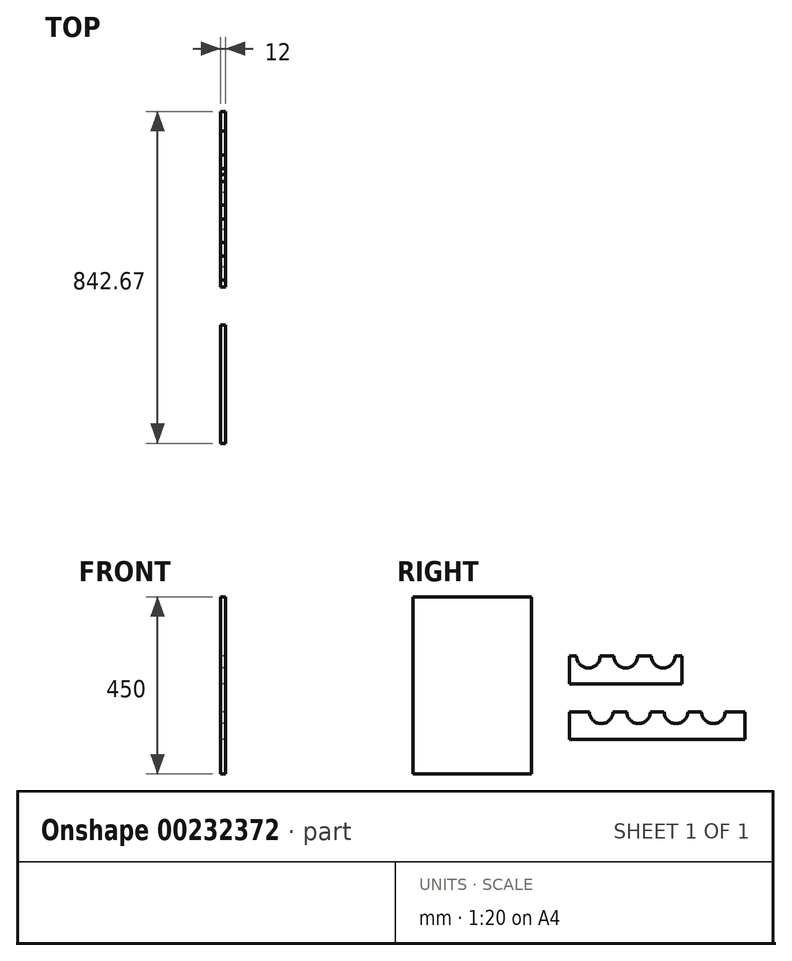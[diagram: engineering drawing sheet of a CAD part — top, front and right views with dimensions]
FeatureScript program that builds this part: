
annotation { "Feature Type Name" : "Feature", "Feature Type Description" : "" }
export const myFeature = defineFeature(function(context is Context, id is Id, definition is map)
    precondition{}
    {
        {
            var Q0;
            Q0=qCreatedBy(makeId("Right.planeOp"),FACE);
            var sketch = newSketch(context, id + "F0", { "sketchPlane" : qUnion([Q0])});
            skLineSegment(sketch, "E0", {"start": v(0, 0) * mm, "end": v(0, 70) * mm});
            skLineSegment(sketch, "E1", {"start": v(0, 70) * mm, "end": v(17.5, 70) * mm});
            skArc(sketch, "E2", {"start": v(17.5, 70) * mm, "mid": v(47.5, 40) * mm, "end": v(77.5, 70) * mm});
            skArc(sketch, "E3.1.0.0", {"start": v(112.5, 70) * mm, "mid": v(142.5, 40) * mm, "end": v(172.5, 70) * mm});
            skArc(sketch, "E3.2.0.0", {"start": v(207.5, 70) * mm, "mid": v(237.5, 40) * mm, "end": v(267.5, 70) * mm});
            skLineSegment(sketch, "E3.direction1", {"start": v(17.5, 70) * mm, "end": v(112.5, 70) * mm, "construction": true});
            skLineSegment(sketch, "E4", {"start": v(77.5, 70) * mm, "end": v(112.5, 70) * mm});
            skLineSegment(sketch, "E5", {"start": v(172.5, 70) * mm, "end": v(207.5, 70) * mm});
            skLineSegment(sketch, "E6", {"start": v(267.5, 70) * mm, "end": v(285, 70) * mm});
            skLineSegment(sketch, "E7", {"start": v(285, 70) * mm, "end": v(285, 0) * mm});
            skLineSegment(sketch, "E8", {"start": v(285, 0) * mm, "end": v(0, 0) * mm});
            skSolve(sketch);
        }
        {
            var Q0;
            Q0 = qSketchRegion(id + "F0", true);
            extrude(context, id + "F1", {"entities" : qUnion([Q0]), "depth" : 12 * mm});
        }
        {
            var Q0;
            Q0=qCreatedBy(makeId("Right.planeOp"),FACE);
            var sketch = newSketch(context, id + "F2", { "sketchPlane" : qUnion([Q0])});
            skLineSegment(sketch, "E9", {"start": v(0, -71.43) * mm, "end": v(0, -141.43) * mm});
            skLineSegment(sketch, "E10", {"start": v(0, -141.43) * mm, "end": v(445, -141.43) * mm});
            skLineSegment(sketch, "E11", {"start": v(445, -141.43) * mm, "end": v(445, -71.43) * mm});
            skLineSegment(sketch, "E12", {"start": v(0, -71.43) * mm, "end": v(50, -71.43) * mm});
            skArc(sketch, "E13", {"start": v(50, -71.43) * mm, "mid": v(80, -101.43) * mm, "end": v(110, -71.43) * mm});
            skArc(sketch, "E14.1.0.0", {"start": v(145, -71.43) * mm, "mid": v(175, -101.43) * mm, "end": v(205, -71.43) * mm});
            skArc(sketch, "E14.2.0.0", {"start": v(240, -71.43) * mm, "mid": v(270, -101.43) * mm, "end": v(300, -71.43) * mm});
            skArc(sketch, "E14.3.0.0", {"start": v(335, -71.43) * mm, "mid": v(365, -101.43) * mm, "end": v(395, -71.43) * mm});
            skLineSegment(sketch, "E14.direction1", {"start": v(50, -71.43) * mm, "end": v(145, -71.43) * mm, "construction": true});
            skLineSegment(sketch, "E15", {"start": v(110, -71.43) * mm, "end": v(145, -71.43) * mm});
            skLineSegment(sketch, "E16", {"start": v(205, -71.43) * mm, "end": v(240, -71.43) * mm});
            skLineSegment(sketch, "E17", {"start": v(300, -71.43) * mm, "end": v(335, -71.43) * mm});
            skLineSegment(sketch, "E18", {"start": v(395, -71.43) * mm, "end": v(445, -71.43) * mm});
            skSolve(sketch);
        }
        {
            var Q0;
            Q0 = qSketchRegion(id + "F2", true);
            extrude(context, id + "F3", {"entities" : qUnion([Q0]), "depth" : 12 * mm});
        }
        {
            var Q0;
            Q0=qCreatedBy(makeId("Right.planeOp"),FACE);
            var sketch = newSketch(context, id + "F4", { "sketchPlane" : qUnion([Q0])});
            skLineSegment(sketch, "E19.bottom", {"start": v(-397.67, -229.24) * mm, "end": v(-97.67, -229.24) * mm});
            skLineSegment(sketch, "E19.top", {"start": v(-397.67, 220.76) * mm, "end": v(-97.67, 220.76) * mm});
            skLineSegment(sketch, "E19.left", {"start": v(-397.67, -229.24) * mm, "end": v(-397.67, 220.76) * mm});
            skLineSegment(sketch, "E19.right", {"start": v(-97.67, -229.24) * mm, "end": v(-97.67, 220.76) * mm});
            skSolve(sketch);
        }
        {
            var Q0;
            Q0=makeQuery(id+"F4.imprint","IMPRINT",FACE,{"disambiguationData":[TD([[makeQuery(id+"F4.imprint","IMPRINT",EDGE,{"derivedFrom":sQuery(id+"F4.wireOp",EDGE,"E19.bottom")}),1.0]])]});
            extrude(context, id + "F5", {"entities" : qUnion([Q0]), "depth" : 12 * mm});
        }
    });
